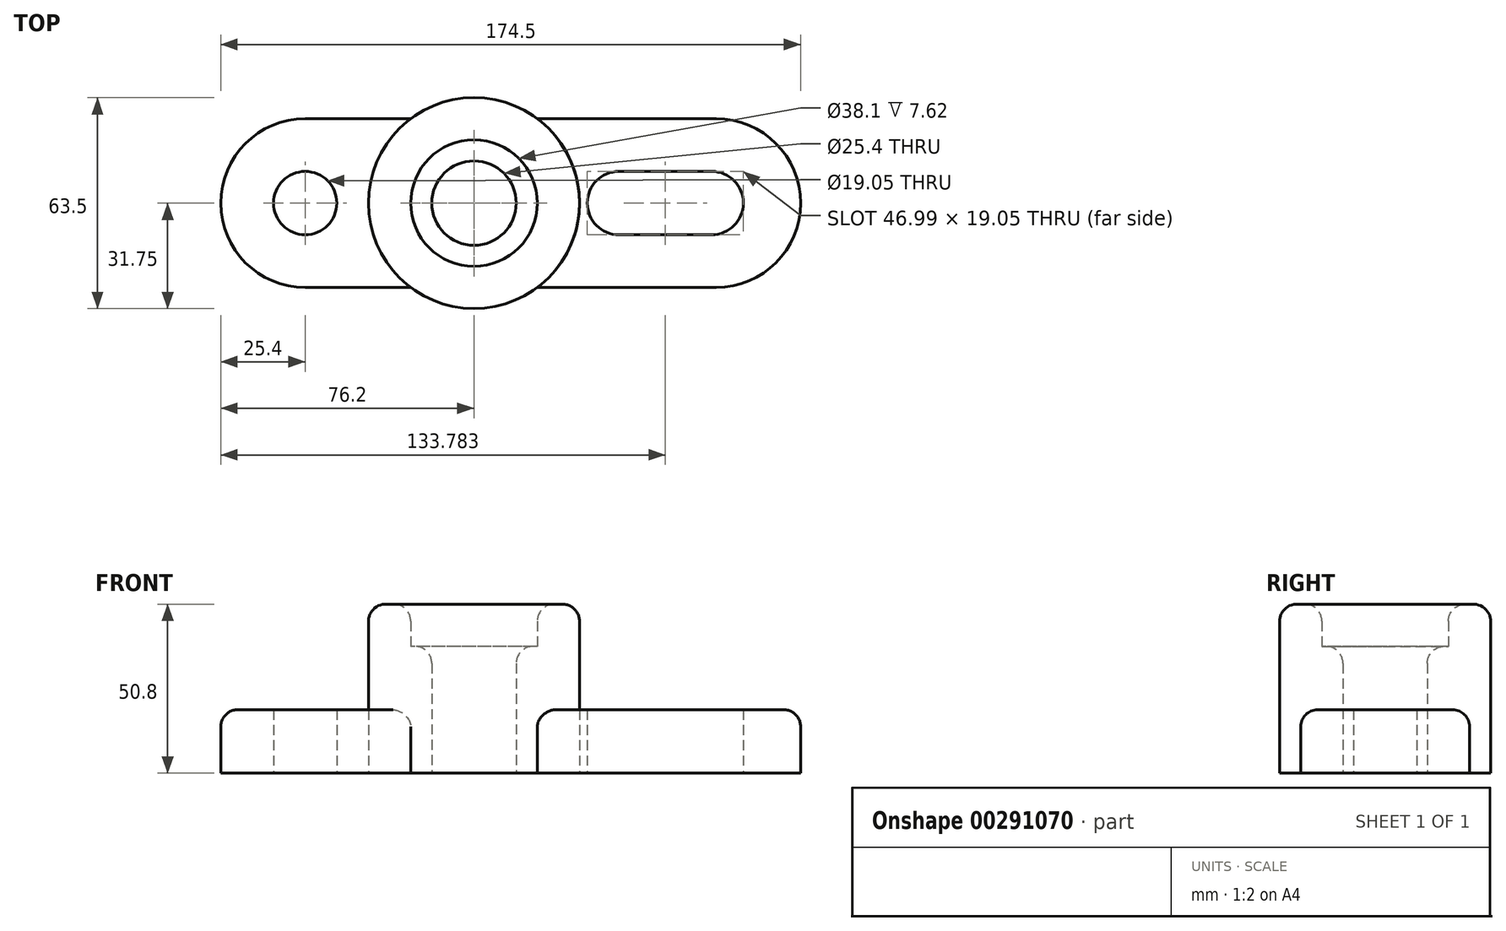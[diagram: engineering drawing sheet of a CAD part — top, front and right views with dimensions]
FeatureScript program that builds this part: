
annotation { "Feature Type Name" : "Feature", "Feature Type Description" : "" }
export const myFeature = defineFeature(function(context is Context, id is Id, definition is map)
    precondition{}
    {
        {
            var Q0;
            Q0=qCreatedBy(makeId("Top.planeOp"),FACE);
            var sketch = newSketch(context, id + "F0", { "sketchPlane" : qUnion([Q0])});
            skCircle(sketch, "E0", {"center": v(0, 0) * mm, "radius": 12.7 * mm});
            skCircle(sketch, "E1", {"center": v(0, 0) * mm, "radius": 19.05 * mm});
            skCircle(sketch, "E2", {"center": v(0, 0) * mm, "radius": 31.75 * mm});
            skLineSegment(sketch, "E3", {"start": v(19.05, 25.4) * mm, "end": v(72.9, 25.4) * mm});
            skLineSegment(sketch, "E4", {"start": v(19.05, -25.4) * mm, "end": v(72.9, -25.4) * mm});
            skLineSegment(sketch, "E5", {"start": v(-19.05, 25.4) * mm, "end": v(-50.8, 25.4) * mm});
            skLineSegment(sketch, "E6", {"start": v(-19.05, -25.4) * mm, "end": v(-50.8, -25.4) * mm});
            skArc(sketch, "E7", {"start": v(72.9, 25.4) * mm, "mid": v(98.3, 0) * mm, "end": v(72.9, -25.4) * mm});
            skArc(sketch, "E8", {"start": v(-50.8, 25.4) * mm, "mid": v(-76.2, 0) * mm, "end": v(-50.8, -25.4) * mm});
            skLineSegment(sketch, "E9.bottom", {"start": v(43.61, 9.52) * mm, "end": v(71.55, 9.52) * mm});
            skLineSegment(sketch, "E9.top", {"start": v(43.61, -9.53) * mm, "end": v(71.55, -9.53) * mm});
            skLineSegment(sketch, "E9.left", {"start": v(43.61, 9.53) * mm, "end": v(43.61, -9.52) * mm});
            skLineSegment(sketch, "E9.right", {"start": v(71.55, 9.53) * mm, "end": v(71.55, -9.52) * mm});
            skPoint(sketch, "E9.middle", {"position": v(57.58, 0) * mm});
            skArc(sketch, "E10", {"start": v(43.61, 9.53) * mm, "mid": v(34.09, 0) * mm, "end": v(43.61, -9.53) * mm});
            skArc(sketch, "E11", {"start": v(71.55, 9.53) * mm, "mid": v(81.08, 0) * mm, "end": v(71.55, -9.53) * mm});
            skCircle(sketch, "E12", {"center": v(-50.8, 0) * mm, "radius": 9.53 * mm});
            skSolve(sketch);
        }
        {
            var Q0;
            Q0=makeQuery(id+"F0.imprint","IMPRINT",FACE,{"disambiguationData":[TD([[makeQuery(id+"F0.imprint","IMPRINT",EDGE,{"derivedFrom":sQuery(id+"F0.wireOp",EDGE,"MNnS6ib6-sHTh-dX0Y-Bbyq-GvMVIUZp1xyQ")}),1.0]])]});
            var Q1;
            {var subQ0=sQuery(id+"F0.wireOp",EDGE,"E5");Q1=makeQuery(id+"F0.imprint","IMPRINT",FACE,{"disambiguationData":[TD([[makeQuery(id+"F0.imprint","IMPRINT",EDGE,{"derivedFrom":subQ0}),1.0]])]});}
            var Q2;
            {var subQ0=sQuery(id+"F0.wireOp",EDGE,"E3");Q2=makeQuery(id+"F0.imprint","IMPRINT",FACE,{"disambiguationData":[TD([[makeQuery(id+"F0.imprint","IMPRINT",EDGE,{"derivedFrom":subQ0}),-1.0]])]});}
            var Q3;
            Q3=makeQuery(id+"F0.imprint","IMPRINT",FACE,{"disambiguationData":[TD([[makeQuery(id+"F0.imprint","IMPRINT",EDGE,{"derivedFrom":sQuery(id+"F0.wireOp",EDGE,"tH666LCN-lF73-HNNL-NMYY-8CVquRXvbQbB")}),1.0]])]});
            extrude(context, id + "F1", {"entities" : qUnion([Q0, Q1, Q2, Q3]), "depth" : 19.05 * mm});
        }
        {
            var Q0;
            Q0=makeQuery(id+"F0.imprint","IMPRINT",FACE,{"disambiguationData":[TD([[makeQuery(id+"F0.imprint","IMPRINT",EDGE,{"derivedFrom":sQuery(id+"F0.wireOp",EDGE,"E1")}),-1.0]])]});
            extrude(context, id + "F2", {"entities" : qUnion([Q0]), "depth" : 50.8 * mm});
        }
        {
            var Q0;
            Q0=makeQuery(id+"F0.imprint","IMPRINT",FACE,{"disambiguationData":[TD([[makeQuery(id+"F0.imprint","IMPRINT",EDGE,{"derivedFrom":sQuery(id+"F0.wireOp",EDGE,"E0")}),-1.0]])]});
            extrude(context, id + "F3", {"entities" : qUnion([Q0]), "operationType" : NewBodyOperationType.ADD, "depth" : 38.1 * mm});
        }
        {
            var Q0;
            Q0=makeQuery(id+"F1.opExtrude","CAP_EDGE",EDGE,{"disambiguationData":[OSD([sQuery(id+"F0.wireOp",EDGE,"E8")])],"isStart":false});
            var Q1;
            Q1=makeQuery(id+"F1.opExtrude","CAP_EDGE",EDGE,{"disambiguationData":[OSD([sQuery(id+"F0.wireOp",EDGE,"E7")])],"isStart":false});
            var Q2;
            Q2=makeQuery(id+"F2.opExtrude","CAP_EDGE",EDGE,{"disambiguationData":[OSD([sQuery(id+"F0.wireOp",EDGE,"E2")])],"isStart":false});
            var Q3;
            Q3=makeQuery(id+"F2.opExtrude","CAP_EDGE",EDGE,{"disambiguationData":[OSD([sQuery(id+"F0.wireOp",EDGE,"E1")])],"isStart":false});
            var Q4;
            Q4=makeQuery(id+"F3.opExtrude","CAP_EDGE",EDGE,{"disambiguationData":[OSD([sQuery(id+"F0.wireOp",EDGE,"E0")])],"isStart":false});
            fillet(context, id + "F4", {"entities" : qUnion([Q0, Q1, Q2, Q3, Q4]), "radius" : 5.08 * mm, "tangentPropagation" : true, "allowEdgeOverflow" : false});
        }
    });
